# Revit family: Domotics-SerieCivili-GEWISS-27COMBI_SYSTEM-IP40_AVVISATORI_ACUSTICI
name_source: partatom
category: Modelli generici
revit_build: Autodesk Revit 2016 (Build: 20161004_0715(x64)
units: mm (PartAtom-declared; Revit-internal decimal feet)

## family parameters
Condiviso = No
Host = Superficie
Punto di calcolo locali = No
Può ospitare armatura = No
Quota connettore circolare = Usa diametro
Taglio con vuoti quando caricato = No
Tipo di parte = Normale

## types (1)
- Domotics-SerieCivili-GEWISS-27COMBI_SYSTEM-IP40_AVVISATORI_ACUSTICI
    Altezza = 800 mm  [stored 2.62467 ft]
    Catalogo = DOMOTICS
    Catalogo Serie = 27COMBI
    Classe isolamento = II
    Codice EAN = 8011564033238
    Codice Electrocod = 0132
    Colore = Grigio RAL 7035
    Descrizione = AVVISATORE ACUSTICO 230V
    Dim. esterne BxHxP (mm) = 64x80x59
    Frequenza impulsi sonori = 1HZ
    Glow Wire Test = 650°C
    Grado di protezione = IP40
    IDF = 77528440-4c1c-495d-97b7-0c6b5e1fb9ad
    IDT = 42373ce3-cb7a-4058-9c9c-5d702b03e44c
    Immagine tipo = GW26427.jpg
    Intensità sonora = 70 dB (a 1 m)
    Larghezza = 640 mm
    Modello = GW26427
    Norma di riferimento = EN 62080
    Produttore = GEWISS S.p.A.
    Profonfità = 590 mm  [stored 1.9357 ft]
    Prospetto di default = 1219 mm
    Scheda Tecnica = https://www.gewiss.com
    Temperatura di installazione = -25 +60 °C
    Tensione nominale = 230 V ac
    Termopressione con biglia = 70 °C
    URL = https://www.gewiss.com
    Versione file RFA = 18.0

note: [stored X ft] marks values corroborated as IEEE doubles in the binary element streams (Revit-internal decimal feet)
